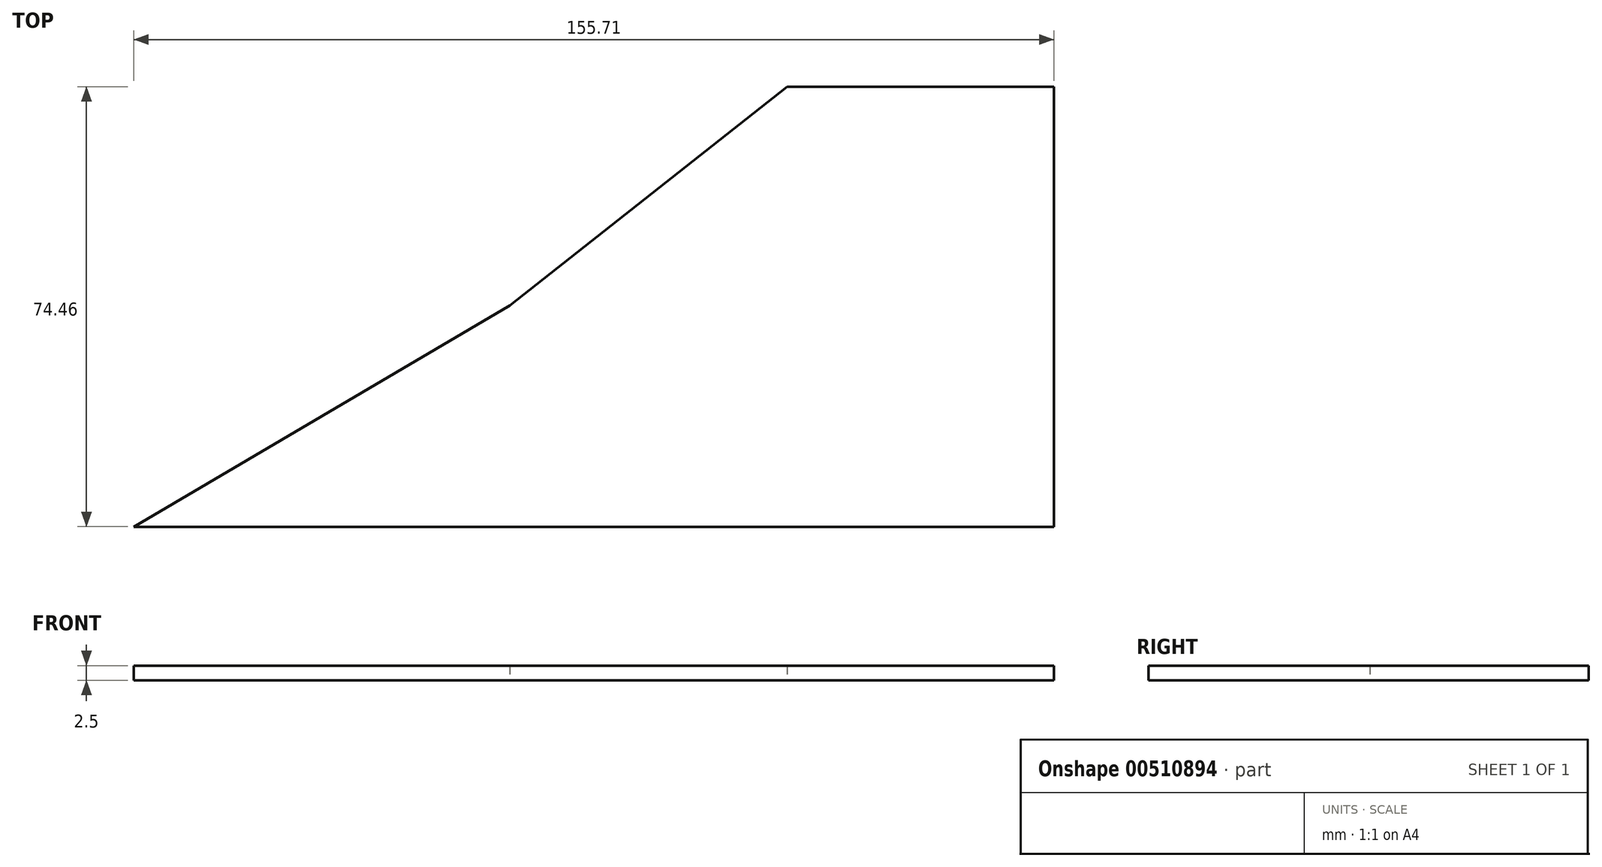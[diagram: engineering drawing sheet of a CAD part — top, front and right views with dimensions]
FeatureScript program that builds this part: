
annotation { "Feature Type Name" : "Feature", "Feature Type Description" : "" }
export const myFeature = defineFeature(function(context is Context, id is Id, definition is map)
    precondition{}
    {
        {
            var Q0;
            Q0=qCreatedBy(makeId("Top.planeOp"),FACE);
            var sketch = newSketch(context, id + "F0", { "sketchPlane" : qUnion([Q0])});
            skLineSegment(sketch, "E0", {"start": v(-75.4, -14.25) * mm, "end": v(80.3, -14.25) * mm});
            skLineSegment(sketch, "E1", {"start": v(80.3, -14.25) * mm, "end": v(80.3, 60.2) * mm});
            skLineSegment(sketch, "E2", {"start": v(80.3, 60.2) * mm, "end": v(35.18, 60.2) * mm});
            skLineSegment(sketch, "E3", {"start": v(35.18, 60.2) * mm, "end": v(-11.76, 23.2) * mm});
            skLineSegment(sketch, "E4", {"start": v(-75.4, -14.25) * mm, "end": v(-11.76, 23.2) * mm});
            skSolve(sketch);
        }
        {
            var Q0;
            Q0=makeQuery(id+"F0.imprint","IMPRINT",FACE,{"disambiguationData":[TD([[makeQuery(id+"F0.imprint","IMPRINT",EDGE,{"derivedFrom":sQuery(id+"F0.wireOp",EDGE,"E0")}),1.0]])]});
            extrude(context, id + "F1", {"entities" : qUnion([Q0]), "depth" : 2.5 * mm, "offsetDistance" : 25 * mm});
        }
    });
